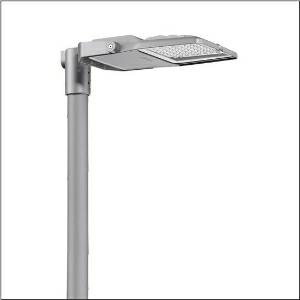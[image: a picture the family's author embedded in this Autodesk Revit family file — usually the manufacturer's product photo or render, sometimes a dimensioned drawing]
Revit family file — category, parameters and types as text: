
# Revit family: floodlight_fl_21_iq_mini___pl64_5xa7772d4e3a_9d14
name_source: partatom
category: Lighting Fixtures
units: mm (PartAtom-declared; Revit-internal decimal feet)

## family parameters
Cut with Voids When Loaded = No
Host = Face
Light Source = No
Part Type = Normal
Room Calculation Point = No
Round Connector Dimension = Use Diameter
Shared = No

## types (1)
- --- (1 x LED, 17970 lm, 143 W, 4000K)
    Apparent Load = 143 VA
    CIE Flux Codes = 28 80 98 100 100
    Color Rendering = 70
    Color Temperature = 4000K
    Default Elevation = 1800 mm
    Description = Floodlight FL 21 iQ mini, floodlight, primary light control with lens, of PMMA, primary optical cover: protective disc, of toughened safety glass, transparent, light distribution: PL64, light emission: direct distribution, installation type: surface-mounted, LED, High Power LED, rated luminous flux: 17.970lm, luminous efficacy: 126lm/W, light colour: 740, colour temperature: 4000K, control gear: iQ Street-Remote/DALI, control: Auto-Match, Temp-Guard, Night-Set, Smart-Wire, Desk-Remote (wireless, voltage-free reading and setting of iQ features in the workshop via application-optimized NFC function/RFID function), optimised constant luminous flux control (CLO 2.0), Light-Fading, Lumen-Switch, with terminal, 6-pole, mains connection: 220..240V, AC, 50/60Hz, start of lifetime: 143W, end of service life: 152W, reduction: 61W, luminaire housing, of diecast aluminium, powder-coated, Siteco® metallic grey (DB 702S), corrosivity category C5 mid according to DIN EN ISO 12944, suitable for swimming pools, chlorine-resistant, sealing non-destructively replaceable, please order mast flange separately, mast bracket, of steel, galvanised, powder-coated, protection rating (complete): IP66, insulation class (complete): insulation class II (safety insulation), certification: CE, ENEC, VDE, protection symbol: D, impact resistance: IK08, permissible operating ambient temperature: -40..+40°C, permissible operating ambient temperature for outdoor applications: -40..+50°C, standard: DIN EN 12944, LABS conformity tested according to VDMA 24364:2018-05, packaging unit: 1 piece

Light Distribution: PL64
    Height = 70 mm
    Lamp = 1 x LED
    Lamp Light Flux = 17970 lm
    Lamp Power = 143 W
    Lamp count = 1
    Length = 485 mm
    Luminous efficacy = 126 lm/W
    Manufacturer = Siteco
    ModVariant = No
    Model = 5XA7772D4E3A
    Number of Poles = 1
    OnlyDefault = Yes
    Power Factor = 1
    Product Name = Floodlight FL 21 iQ mini | PL64
    Product group = floodlight | pylon annexe
    ProductGroupID = 6200
    Protection Class = Protection class II
    Protection Degree = IP 66
    RLX_Detail_Level = 1
    RLX_Emergency_Light_Flux = 0 lm
    RLX_Emergency_Type = 0
    RLX_Emergency_Type_DB = No
    RlxData = <blob elided: 101709 chars, md5=fd078aa2>
    Socket = socket
    Standby Power = 0 W
    System Light Flux = 17970 lm
    System Power = 143 W
    Type Comments = factory setting: luminous flux: 100 % | dim-lin: 254 | 730 mA
    Type Image = l_1007125.jpg
    URL = http://relux.com
    VarID = @adj_165650
    Voltage = 0 V
    Weight = 0.00 kg
    Width = 337 mm

## geometry (parser evidence)
native form markers: Blend x4, Sweep x10
no freeform markers — native parametric forms only
